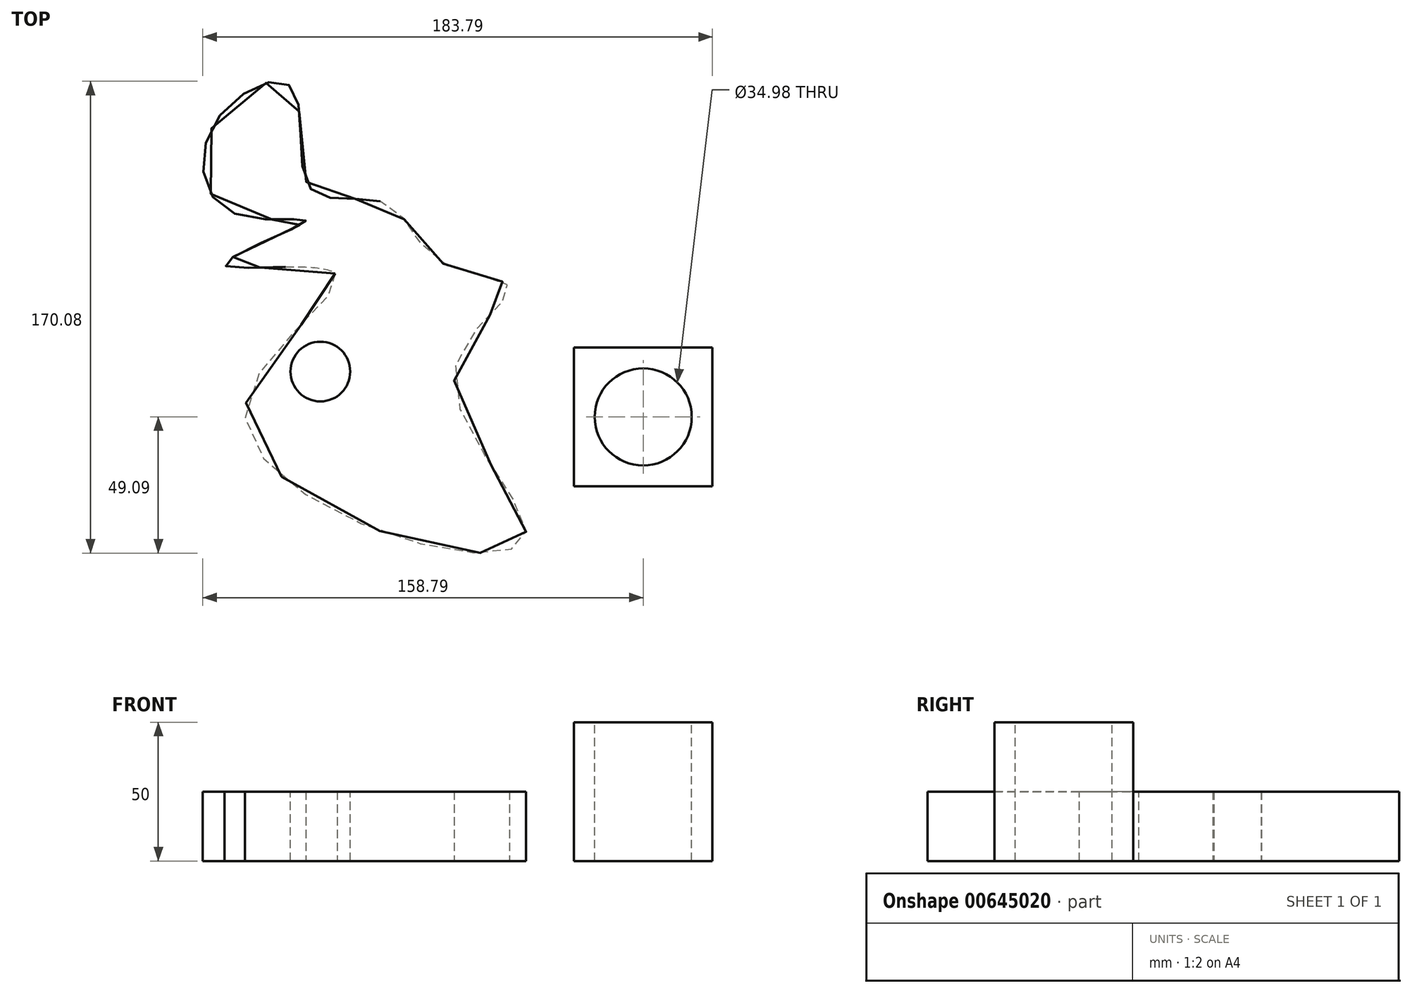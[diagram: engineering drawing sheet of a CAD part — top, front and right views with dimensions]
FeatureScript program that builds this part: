
annotation { "Feature Type Name" : "Feature", "Feature Type Description" : "" }
export const myFeature = defineFeature(function(context is Context, id is Id, definition is map)
    precondition{}
    {
        {
            var Q0;
            Q0=qCreatedBy(makeId("Top.planeOp"),FACE);
            var sketch = newSketch(context, id + "F0", { "sketchPlane" : qUnion([Q0])});
            skLineSegment(sketch, "E0.bottom", {"start": v(-25, -25) * mm, "end": v(25, -25) * mm});
            skLineSegment(sketch, "E0.top", {"start": v(-25, 25) * mm, "end": v(25, 25) * mm});
            skLineSegment(sketch, "E0.left", {"start": v(-25, -25) * mm, "end": v(-25, 25) * mm});
            skLineSegment(sketch, "E0.right", {"start": v(25, -25) * mm, "end": v(25, 25) * mm});
            skPoint(sketch, "E0.middle", {"position": v(0, 0) * mm});
            skSolve(sketch);
        }
        {
            var Q0;
            Q0 = qSketchRegion(id + "F0", true);
            extrude(context, id + "F1", {"entities" : qUnion([Q0]), "depth" : 50 * mm, "offsetDistance" : 25 * mm});
        }
        {
            var Q0;
            Q0=makeQuery(id+"F1.opExtrude","CAP_FACE",FACE,{"disambiguationData":[OSD([sQuery(id+"F0.wireOp",EDGE,"E0.bottom"),sQuery(id+"F0.wireOp",EDGE,"E0.top"),sQuery(id+"F0.wireOp",EDGE,"E0.left"),sQuery(id+"F0.wireOp",EDGE,"E0.right")])],"isStart":false});
            var sketch = newSketch(context, id + "F2", { "sketchPlane" : qUnion([Q0])});
            skCircle(sketch, "E1", {"center": v(0, 0) * mm, "radius": 17.49 * mm});
            skSolve(sketch);
        }
        {
            var Q0;
            Q0=makeQuery(id+"F2.imprint","IMPRINT",FACE,{"disambiguationData":[TD([[makeQuery(id+"F2.imprint","IMPRINT",EDGE,{"derivedFrom":sQuery(id+"F2.wireOp",EDGE,"E1")}),1.0]])]});
            extrude(context, id + "F3", {"entities" : qUnion([Q0]), "operationType" : NewBodyOperationType.REMOVE, "oppositeDirection" : true, "depth" : 50 * mm, "offsetDistance" : 25 * mm});
        }
        {
            var Q0;
            Q0=qCreatedBy(makeId("Top.planeOp"),FACE);
            var sketch = newSketch(context, id + "F4", { "sketchPlane" : qUnion([Q0])});
            skFitSpline(sketch, "E2", {"points": [v(-111.07, 51.7) * mm, v(-143.04, 5.86) * mm, v(-82.06, -45.2) * mm, v(-42.23, -41.4) * mm, v(-68.1, 15.7) * mm, v(-48.2, 46.45) * mm, v(-73.15, 55.85) * mm, v(-93, 77.16) * mm, v(-120.16, 82.51) * mm, v(-127.1, 119.16) * mm, v(-155.08, 105.04) * mm, v(-147.81, 73.47) * mm, v(-121.81, 70.49) * mm, v(-150.94, 54.9) * mm, v(-111.07, 51.7) * mm]});
            skSolve(sketch);
        }
        {
            var Q0;
            Q0=makeQuery(id+"F4.imprint","IMPRINT",FACE,{"disambiguationData":[TD([[makeQuery(id+"F4.imprint","IMPRINT",EDGE,{"derivedFrom":sQuery(id+"F4.wireOp",EDGE,"E2")}),1.0]])]});
            extrude(context, id + "F5", {"entities" : qUnion([Q0]), "depth" : 25 * mm, "offsetDistance" : 25 * mm});
        }
        {
            var Q0;
            Q0=makeQuery(id+"F5.opExtrude","CAP_FACE",FACE,{"disambiguationData":[OSD([sQuery(id+"F4.wireOp",EDGE,"E2")])],"isStart":false});
            var sketch = newSketch(context, id + "F6", { "sketchPlane" : qUnion([Q0])});
            skCircle(sketch, "E3", {"center": v(-116.4, 16.35) * mm, "radius": 10.77 * mm});
            skSolve(sketch);
        }
        {
            var Q0;
            Q0 = qSketchRegion(id + "F6", true);
            extrude(context, id + "F7", {"entities" : qUnion([Q0]), "operationType" : NewBodyOperationType.REMOVE, "oppositeDirection" : true, "depth" : 25 * mm, "offsetDistance" : 25 * mm});
        }
    });
